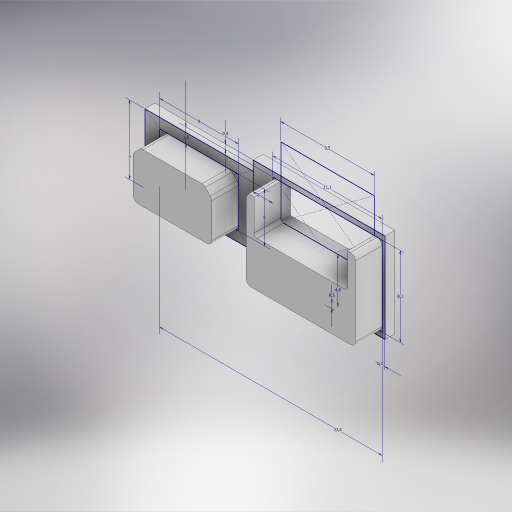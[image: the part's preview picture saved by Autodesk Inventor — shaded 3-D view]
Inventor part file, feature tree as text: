
AUTODESK INVENTOR PART (.ipt)
format: ipt  version: 2024 (Build 280153000, 153)  size: 398,848 bytes
history: native  units: mm
features: extrude x4, other x3, fillet x3, sketch x1, chamfer x1
ambient origin geometry x8: Origin, YZ Plane, XZ Plane, XY Plane, X Axis, Y Axis, Z Axis, Center Point
bodies: Solid1 (feature_tree)
feature tree (12):
  other  "Table"
  other  "firewire-01"
  other  "firewire combo"
  sketch  "Sketch1"  dims[d0=11.1mm d1=8.1mm d2=9.5mm d3=4.6mm d4=2.7mm d5=0.0mm d6=0.5mm d7=0.3mm d8=0.5mm d9=2.0mm d10=0.5mm d11=0.3mm d12=1.0mm d13=0.0mm d14=8.0mm d15=5.0mm d16=1.5mm d17=22.6mm d18=7.0mm d19=1.0mm d20=0.0mm d21=1.0mm d22=0.0mm d23=0.8mm d24=2.0mm d25=45.0deg d26=0.5mm d27=0.5mm d28=0.872665mm d29=0.5mm d30=0.872665mm]
  extrude  "Extrusion1"  Depth=8.1mm
  fillet  "Fillet1"  Radius=9.5mm
  fillet  "Fillet2"  Radius=4.6mm
  extrude  "Extrusion2"  Depth=2.7mm TaperAngle=0.0deg
  extrude  "Extrusion3"  Depth=0.5mm
  extrude  "Extrusion4"  Depth=0.3mm
  chamfer  "Chamfer1"  Distance=0.5mm
  fillet  "Fillet3"  Radius=2.0mm
